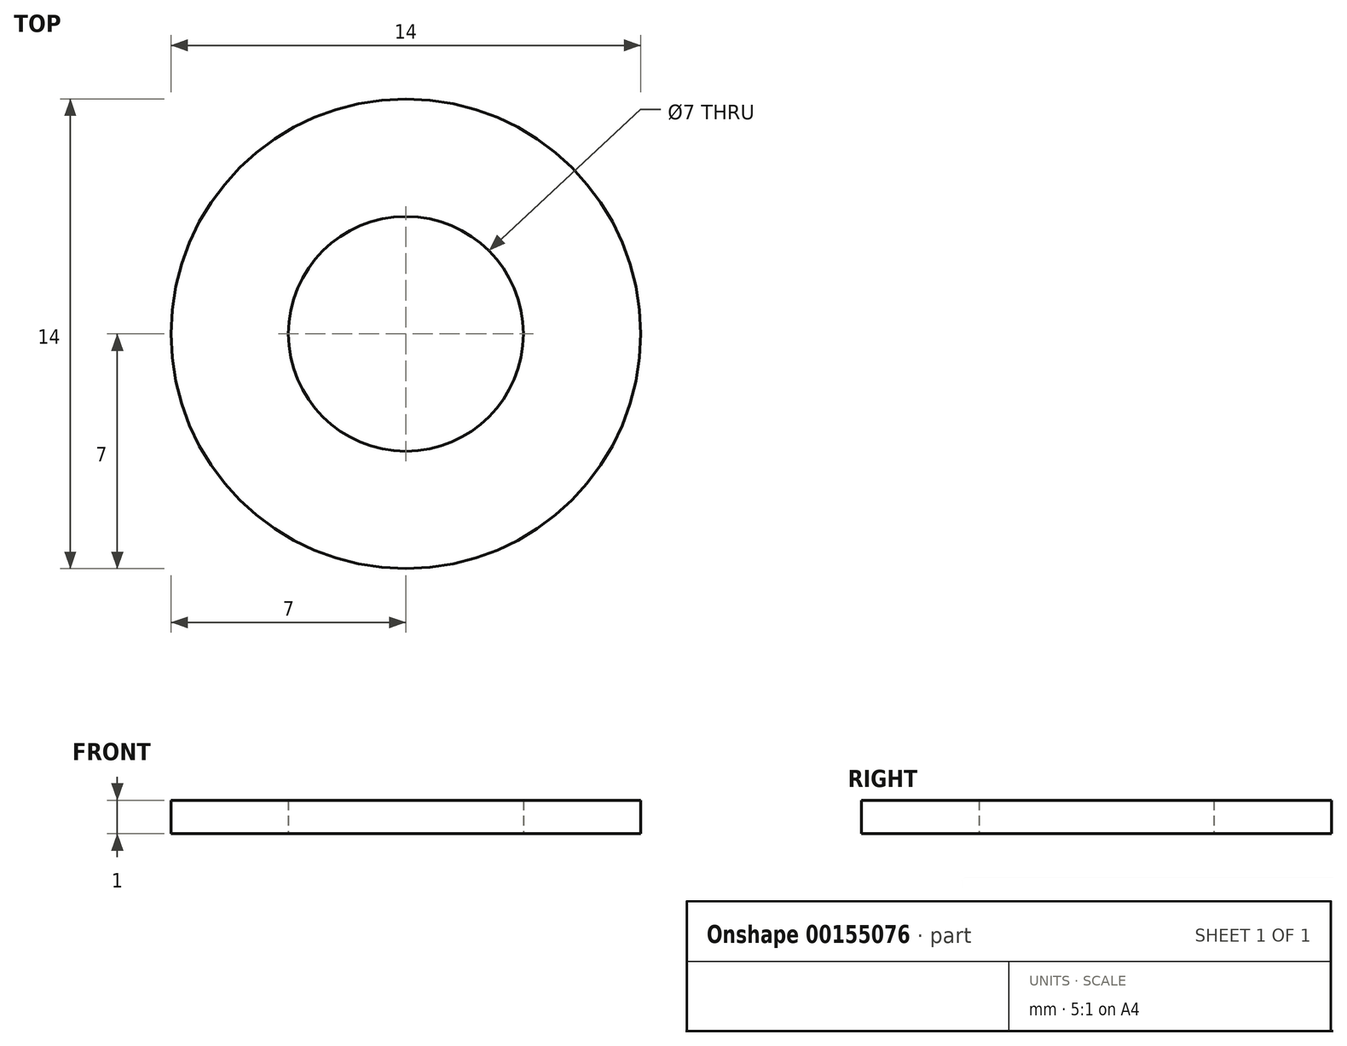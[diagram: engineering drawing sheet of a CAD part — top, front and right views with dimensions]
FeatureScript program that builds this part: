
annotation { "Feature Type Name" : "Feature", "Feature Type Description" : "" }
export const myFeature = defineFeature(function(context is Context, id is Id, definition is map)
    precondition{}
    {
        {
            var Q0;
            Q0=qCreatedBy(makeId("Top.planeOp"),FACE);
            var sketch = newSketch(context, id + "F0", { "sketchPlane" : qUnion([Q0])});
            skCircle(sketch, "E0", {"center": v(0, 0) * mm, "radius": 7 * mm});
            skCircle(sketch, "E1", {"center": v(0, 0) * mm, "radius": 3.5 * mm});
            skSolve(sketch);
        }
        {
            var Q0;
            Q0=makeQuery(id+"F0.imprint","IMPRINT",FACE,{"disambiguationData":[TD([[makeQuery(id+"F0.imprint","IMPRINT",EDGE,{"derivedFrom":sQuery(id+"F0.wireOp",EDGE,"E0")}),1.0]])]});
            extrude(context, id + "F1", {"entities" : qUnion([Q0]), "depth" : 1 * mm});
        }
    });
